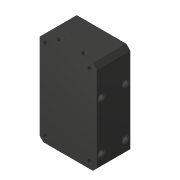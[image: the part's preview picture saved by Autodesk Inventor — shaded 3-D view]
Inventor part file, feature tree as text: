
AUTODESK INVENTOR PART (.ipt)
format: ipt  version: 2019.4 (Build 234330000, 330)  size: 340,992 bytes
history: native  units: mm
features: extrude x7, sketch x7, chamfer x2, other x1, mirror x1
ambient origin geometry x8: Origin, YZ Plane, XZ Plane, XY Plane, X Axis, Y Axis, Z Axis, Center Point
bodies: Body1 (feature_tree)
feature tree (18):
  other  "ソリッド1"
  extrude  "押し出し1"  Depth=11.25mm
  extrude  "押し出し2"  Depth=28.5mm
  mirror  "ミラー1"
  extrude  "押し出し3"  Depth=46.5mm
  extrude  "押し出し4"  Depth=2.0mm
  chamfer  "面取り1"  Distance=2.0mm
  chamfer  "面取り2"  Distance=2.0mm
  extrude  "押し出し5"  Depth=2.0mm
  extrude  "押し出し7"  Depth=2.0mm
  extrude  "押し出し6"  Depth=2.0mm
  sketch  "スケッチ1"
  sketch  "スケッチ2"
  sketch  "スケッチ3"
  sketch  "スケッチ4"
  sketch  "スケッチ5"
  sketch  "スケッチ6"
  sketch  "スケッチ7"
